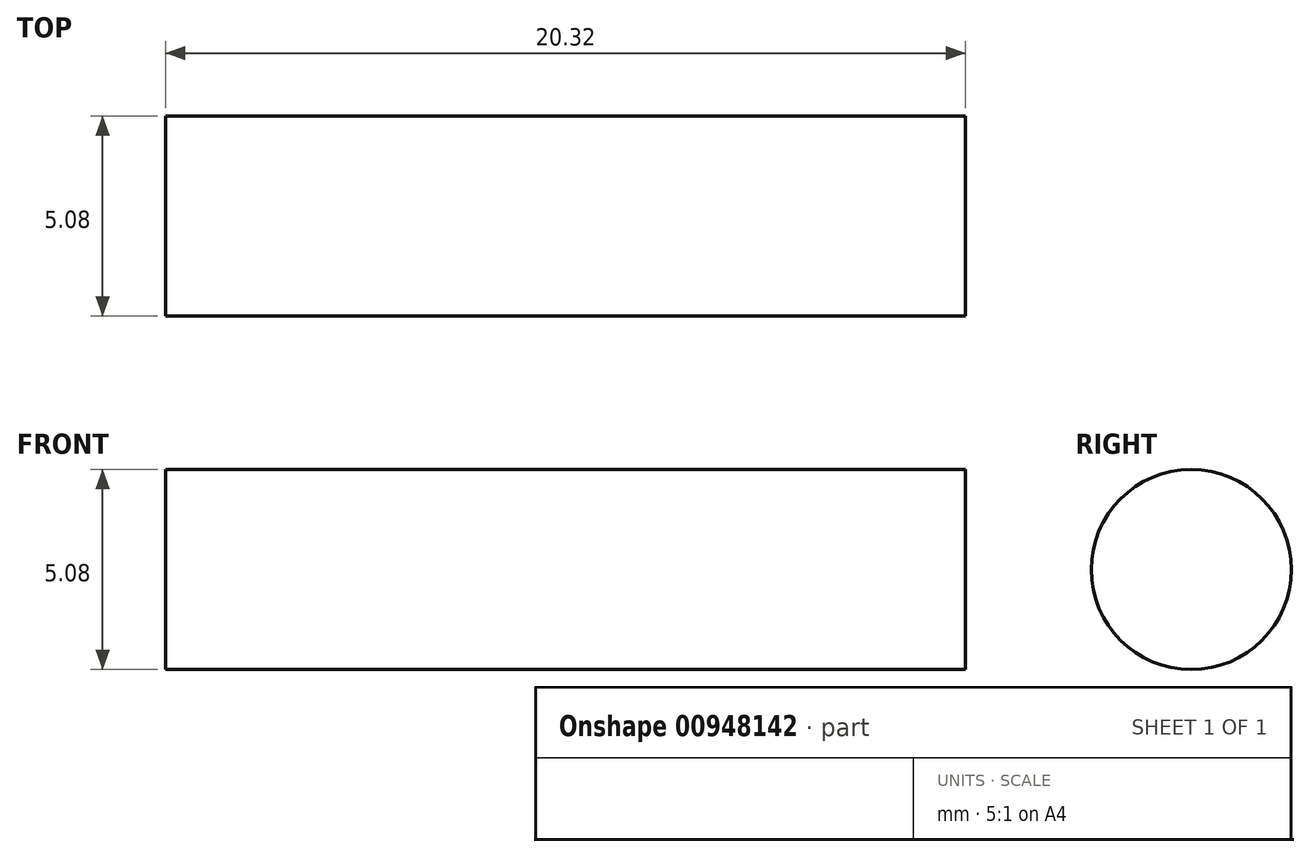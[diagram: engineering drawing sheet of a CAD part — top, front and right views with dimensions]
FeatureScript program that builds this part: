
annotation { "Feature Type Name" : "Feature", "Feature Type Description" : "" }
export const myFeature = defineFeature(function(context is Context, id is Id, definition is map)
    precondition{}
    {
        {
            var Q0;
            Q0=qCreatedBy(makeId("Right.planeOp"),FACE);
            var sketch = newSketch(context, id + "F0", { "sketchPlane" : qUnion([Q0])});
            skCircle(sketch, "E0", {"center": v(-40, 35.5) * mm, "radius": 2.54 * mm});
            skSolve(sketch);
        }
        {
            var Q0;
            Q0=makeQuery(id+"F0.imprint","IMPRINT",FACE,{"disambiguationData":[TD([[makeQuery(id+"F0.imprint","IMPRINT",EDGE,{"derivedFrom":sQuery(id+"F0.wireOp",EDGE,"E0")}),1.0]])]});
            extrude(context, id + "F1", {"entities" : qUnion([Q0]), "depth" : 20.32 * mm, "offsetDistance" : 25.4 * mm});
        }
    });
